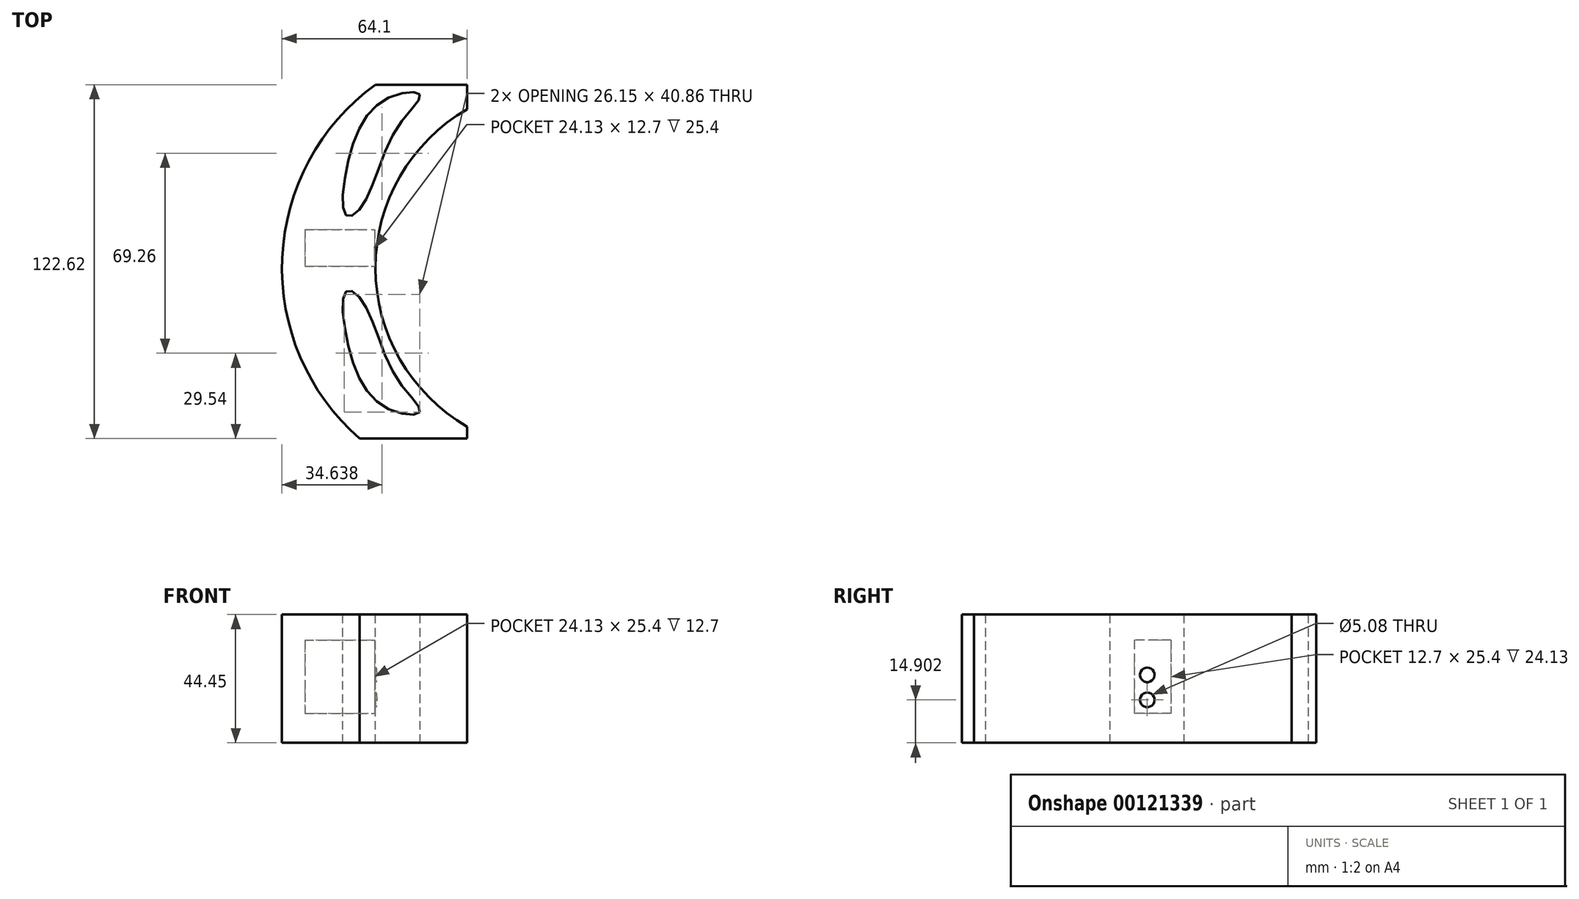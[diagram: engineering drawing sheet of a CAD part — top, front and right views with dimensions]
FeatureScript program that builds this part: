
annotation { "Feature Type Name" : "Feature", "Feature Type Description" : "" }
export const myFeature = defineFeature(function(context is Context, id is Id, definition is map)
    precondition{}
    {
        {
            var Q0;
            Q0=qCreatedBy(makeId("Top.planeOp"),FACE);
            var sketch = newSketch(context, id + "F0", { "sketchPlane" : qUnion([Q0])});
            skLineSegment(sketch, "E0.bottom", {"start": v(-63.24, 58.45) * mm, "end": v(63.76, 58.45) * mm});
            skLineSegment(sketch, "E0.top", {"start": v(-63.24, -68.55) * mm, "end": v(63.76, -68.55) * mm});
            skLineSegment(sketch, "E0.left", {"start": v(-63.24, 58.45) * mm, "end": v(-63.24, -68.55) * mm});
            skLineSegment(sketch, "E0.right", {"start": v(63.76, 58.45) * mm, "end": v(63.76, -68.55) * mm});
            skSolve(sketch);
        }
        {
            var Q0;
            Q0 = qSketchRegion(id + "F0", true);
            extrude(context, id + "F1", {"entities" : qUnion([Q0]), "depth" : 44.45 * mm});
        }
        {
            var Q0;
            Q0=makeQuery(id+"F1.opExtrude","CAP_FACE",FACE,{"disambiguationData":[OSD([sQuery(id+"F0.wireOp",EDGE,"E0.bottom"),sQuery(id+"F0.wireOp",EDGE,"E0.top"),sQuery(id+"F0.wireOp",EDGE,"E0.left"),sQuery(id+"F0.wireOp",EDGE,"E0.right")])],"isStart":false});
            var sketch = newSketch(context, id + "F2", { "sketchPlane" : qUnion([Q0])});
            skPoint(sketch, "E1.startSnap0", {"position": v(0.26, 58.45) * mm});
            skLineSegment(sketch, "E2", {"start": v(-63.24, 58.45) * mm, "end": v(-63.24, -68.55) * mm});
            skLineSegment(sketch, "E3", {"start": v(-63.24, -68.55) * mm, "end": v(0.26, -68.55) * mm});
            skArc(sketch, "E4", {"start": v(0.26, 58.45) * mm, "mid": v(-32.09, -5.05) * mm, "end": v(0.26, -68.55) * mm});
            skLineSegment(sketch, "E5", {"start": v(-63.24, 58.45) * mm, "end": v(0.26, 58.45) * mm});
            skSolve(sketch);
        }
        {
            var Q0;
            Q0 = qSketchRegion(id + "F2", true);
            var Q1;
            Q1=makeQuery(id+"F1.opExtrude","CAP_FACE",FACE,{"disambiguationData":[OSD([sQuery(id+"F0.wireOp",EDGE,"E0.bottom"),sQuery(id+"F0.wireOp",EDGE,"E0.top"),sQuery(id+"F0.wireOp",EDGE,"E0.left"),sQuery(id+"F0.wireOp",EDGE,"E0.right")])],"isStart":true});
            extrude(context, id + "F3", {"entities" : qUnion([Q0]), "operationType" : NewBodyOperationType.REMOVE, "endBound" : BoundingType.UP_TO_SURFACE, "oppositeDirection" : true, "endBoundEntityFace" : qUnion([Q1]), "depth" : 25.4 * mm});
        }
        {
            var Q0;
            Q0=makeQuery(id+"F1.opExtrude","CAP_FACE",FACE,{"disambiguationData":[OSD([sQuery(id+"F0.wireOp",EDGE,"E0.bottom"),sQuery(id+"F0.wireOp",EDGE,"E0.top"),sQuery(id+"F0.wireOp",EDGE,"E0.left"),sQuery(id+"F0.wireOp",EDGE,"E0.right")])],"isStart":false});
            var sketch = newSketch(context, id + "F4", { "sketchPlane" : qUnion([Q0])});
            skArc(sketch, "E6", {"start": v(63.76, 58.45) * mm, "mid": v(0.26, -5.05) * mm, "end": v(63.76, -68.55) * mm});
            skLineSegment(sketch, "E7", {"start": v(63.76, -68.55) * mm, "end": v(63.76, 58.45) * mm});
            skSolve(sketch);
        }
        {
            var Q0;
            Q0 = qSketchRegion(id + "F4", true);
            var Q1;
            Q1=makeQuery(id+"F1.opExtrude","CAP_FACE",FACE,{"disambiguationData":[OSD([sQuery(id+"F0.wireOp",EDGE,"E0.bottom"),sQuery(id+"F0.wireOp",EDGE,"E0.top"),sQuery(id+"F0.wireOp",EDGE,"E0.left"),sQuery(id+"F0.wireOp",EDGE,"E0.right")])],"isStart":true});
            extrude(context, id + "F5", {"entities" : qUnion([Q0]), "operationType" : NewBodyOperationType.REMOVE, "endBound" : BoundingType.UP_TO_SURFACE, "oppositeDirection" : true, "endBoundEntityFace" : qUnion([Q1]), "depth" : 25.4 * mm});
        }
        {
            var Q0;
            Q0=makeQuery(id+"F1.opExtrude","CAP_FACE",FACE,{"disambiguationData":[OSD([sQuery(id+"F0.wireOp",EDGE,"E0.bottom"),sQuery(id+"F0.wireOp",EDGE,"E0.top"),sQuery(id+"F0.wireOp",EDGE,"E0.left"),sQuery(id+"F0.wireOp",EDGE,"E0.right")])],"isStart":false});
            var sketch = newSketch(context, id + "F6", { "sketchPlane" : qUnion([Q0])});
            skLineSegment(sketch, "E8.bottom", {"start": v(45.03, -99.41) * mm, "end": v(83.6, -99.41) * mm});
            skLineSegment(sketch, "E8.top", {"start": v(45.03, 124.65) * mm, "end": v(83.6, 124.65) * mm});
            skLineSegment(sketch, "E8.left", {"start": v(45.03, -99.41) * mm, "end": v(45.03, 124.65) * mm});
            skLineSegment(sketch, "E8.right", {"start": v(83.6, -99.41) * mm, "end": v(83.6, 124.65) * mm});
            skSolve(sketch);
        }
        {
            var Q0;
            {var subQ1=sQuery(id+"F6.wireOp",EDGE,"E8.bottom");Q0=makeQuery(id+"F6.imprint","IMPRINT",FACE,{"disambiguationData":[TD([[makeQuery(id+"F6.imprint","IMPRINT",EDGE,{"derivedFrom":subQ1}),1.0]])]});}
            extrude(context, id + "F7", {"entities" : qUnion([Q0]), "operationType" : NewBodyOperationType.REMOVE, "oppositeDirection" : true, "depth" : 46.07 * mm});
        }
        {
            var Q0;
            Q0=makeQuery(id+"F1.opExtrude","CAP_FACE",FACE,{"disambiguationData":[OSD([sQuery(id+"F0.wireOp",EDGE,"E0.bottom"),sQuery(id+"F0.wireOp",EDGE,"E0.top"),sQuery(id+"F0.wireOp",EDGE,"E0.left"),sQuery(id+"F0.wireOp",EDGE,"E0.right")])],"isStart":false});
            var sketch = newSketch(context, id + "F8", { "sketchPlane" : qUnion([Q0])});
            skLineSegment(sketch, "E9.bottom", {"start": v(32.01, -68.55) * mm, "end": v(64.03, -68.55) * mm});
            skLineSegment(sketch, "E9.top", {"start": v(32.01, -59.64) * mm, "end": v(64.03, -59.64) * mm});
            skLineSegment(sketch, "E9.left", {"start": v(32.01, -68.55) * mm, "end": v(32.01, -59.64) * mm});
            skLineSegment(sketch, "E9.right", {"start": v(64.03, -68.55) * mm, "end": v(64.03, -59.64) * mm});
            skSolve(sketch);
        }
        {
            var Q0;
            Q0 = qSketchRegion(id + "F8", true);
            var Q1;
            Q1=makeQuery(id+"F1.opExtrude","CAP_FACE",FACE,{"disambiguationData":[OSD([sQuery(id+"F0.wireOp",EDGE,"E0.bottom"),sQuery(id+"F0.wireOp",EDGE,"E0.top"),sQuery(id+"F0.wireOp",EDGE,"E0.left"),sQuery(id+"F0.wireOp",EDGE,"E0.right")])],"isStart":true});
            extrude(context, id + "F9", {"entities" : qUnion([Q0]), "operationType" : NewBodyOperationType.REMOVE, "endBound" : BoundingType.UP_TO_SURFACE, "oppositeDirection" : true, "endBoundEntityFace" : qUnion([Q1]), "depth" : 25.4 * mm});
        }
        {
            var Q0;
            Q0=makeQuery(id+"F1.opExtrude","CAP_FACE",FACE,{"disambiguationData":[OSD([sQuery(id+"F0.wireOp",EDGE,"E0.bottom"),sQuery(id+"F0.wireOp",EDGE,"E0.top"),sQuery(id+"F0.wireOp",EDGE,"E0.left"),sQuery(id+"F0.wireOp",EDGE,"E0.right")])],"isStart":false});
            var sketch = newSketch(context, id + "F10", { "sketchPlane" : qUnion([Q0])});
            skLineSegment(sketch, "E10.bottom", {"start": v(32.01, 58.45) * mm, "end": v(63.76, 58.45) * mm});
            skLineSegment(sketch, "E10.top", {"start": v(32.01, 38.53) * mm, "end": v(63.76, 38.53) * mm});
            skLineSegment(sketch, "E10.left", {"start": v(32.01, 58.45) * mm, "end": v(32.01, 38.53) * mm});
            skLineSegment(sketch, "E10.right", {"start": v(63.76, 58.45) * mm, "end": v(63.76, 38.53) * mm});
            skSolve(sketch);
        }
        {
            var Q0;
            Q0 = qSketchRegion(id + "F10", true);
            var Q1;
            Q1=makeQuery(id+"F1.opExtrude","CAP_FACE",FACE,{"disambiguationData":[OSD([sQuery(id+"F0.wireOp",EDGE,"E0.bottom"),sQuery(id+"F0.wireOp",EDGE,"E0.top"),sQuery(id+"F0.wireOp",EDGE,"E0.left"),sQuery(id+"F0.wireOp",EDGE,"E0.right")])],"isStart":true});
            extrude(context, id + "F11", {"entities" : qUnion([Q0]), "operationType" : NewBodyOperationType.REMOVE, "endBound" : BoundingType.UP_TO_SURFACE, "oppositeDirection" : true, "endBoundEntityFace" : qUnion([Q1]), "depth" : 25.4 * mm});
        }
        {
            var Q0;
            Q0=qCreatedBy(makeId("Right.planeOp"),FACE);
            var sketch = newSketch(context, id + "F12", { "sketchPlane" : qUnion([Q0])});
            skLineSegment(sketch, "E11.bottom", {"start": v(8.2, 35.56) * mm, "end": v(-4.5, 35.56) * mm});
            skLineSegment(sketch, "E11.top", {"start": v(8.2, 10.16) * mm, "end": v(-4.5, 10.16) * mm});
            skLineSegment(sketch, "E11.left", {"start": v(8.2, 35.56) * mm, "end": v(8.2, 10.16) * mm});
            skLineSegment(sketch, "E11.right", {"start": v(-4.5, 35.56) * mm, "end": v(-4.5, 10.16) * mm});
            skSolve(sketch);
        }
        {
            var Q0;
            Q0 = qSketchRegion(id + "F12", true);
            var Q1;
            Q1=makeQuery(id+"F3.boolean.opBoolean","COPY",FACE,{"derivedFrom":makeQuery(id+"F3.opExtrude","SWEPT_FACE",FACE,{"disambiguationData":[OSD([sQuery(id+"F2.wireOp",EDGE,"E1")])]})});
            extrude(context, id + "F13", {"entities" : qUnion([Q0]), "operationType" : NewBodyOperationType.REMOVE, "oppositeDirection" : true, "endBoundEntityFace" : qUnion([Q1]), "depth" : 24.13 * mm});
        }
        {
            var Q0;
            Q0=makeQuery(id+"F13.boolean.opBoolean","COPY",FACE,{"derivedFrom":makeQuery(id+"F13.opExtrude","CAP_FACE",FACE,{"disambiguationData":[OSD([sQuery(id+"F12.wireOp",EDGE,"E11.bottom"),sQuery(id+"F12.wireOp",EDGE,"E11.top"),sQuery(id+"F12.wireOp",EDGE,"E11.left"),sQuery(id+"F12.wireOp",EDGE,"E11.right")])],"isStart":true})});
            var sketch = newSketch(context, id + "F14", { "sketchPlane" : qUnion([Q0])});
            skCircle(sketch, "E12", {"center": v(0, 14.9) * mm, "radius": 2.54 * mm});
            skCircle(sketch, "E13", {"center": v(0, 23.56) * mm, "radius": 2.53 * mm});
            skSolve(sketch);
        }
        {
            var Q0;
            Q0 = qSketchRegion(id + "F14", true);
            extrude(context, id + "F15", {"entities" : qUnion([Q0]), "operationType" : NewBodyOperationType.REMOVE, "oppositeDirection" : true, "depth" : 25.4 * mm});
        }
        {
            var Q0;
            Q0=makeQuery(id+"F1.opExtrude","CAP_FACE",FACE,{"disambiguationData":[OSD([sQuery(id+"F0.wireOp",EDGE,"E0.bottom"),sQuery(id+"F0.wireOp",EDGE,"E0.top"),sQuery(id+"F0.wireOp",EDGE,"E0.left"),sQuery(id+"F0.wireOp",EDGE,"E0.right")])],"isStart":true});
            var sketch = newSketch(context, id + "F16", { "sketchPlane" : qUnion([Q0])});
            skFitSpline(sketch, "E14", {"points": [v(15.62, -55.06) * mm, v(3.77, -53.45) * mm, v(-8.86, -33.07) * mm, v(-9.85, -13.16) * mm, v(-4.4, -16.29) * mm, v(7.7, -43.33) * mm, v(15.62, -55.06) * mm]});
            skFitSpline(sketch, "E15.MirrorC", {"points": [v(15.62, 55.06) * mm, v(3.77, 53.45) * mm, v(-8.86, 33.07) * mm, v(-9.85, 13.16) * mm, v(-4.4, 16.29) * mm, v(7.7, 43.33) * mm, v(15.62, 55.06) * mm]});
            skSolve(sketch);
        }
        {
            var Q0;
            Q0 = qSketchRegion(id + "F16", true);
            extrude(context, id + "F17", {"entities" : qUnion([Q0]), "operationType" : NewBodyOperationType.REMOVE, "endBound" : BoundingType.UP_TO_NEXT, "oppositeDirection" : true, "depth" : 25.4 * mm});
        }
        {
            var Q0;
            Q0=makeQuery(id+"F1.opExtrude","CAP_FACE",FACE,{"disambiguationData":[OSD([sQuery(id+"F0.wireOp",EDGE,"E0.bottom"),sQuery(id+"F0.wireOp",EDGE,"E0.top"),sQuery(id+"F0.wireOp",EDGE,"E0.left"),sQuery(id+"F0.wireOp",EDGE,"E0.right")])],"isStart":false});
            var sketch = newSketch(context, id + "F18", { "sketchPlane" : qUnion([Q0])});
            skLineSegment(sketch, "E16.bottom", {"start": v(32.01, -68.55) * mm, "end": v(-12.9, -68.55) * mm});
            skLineSegment(sketch, "E16.top", {"start": v(32.01, -64.17) * mm, "end": v(-12.9, -64.17) * mm});
            skLineSegment(sketch, "E16.left", {"start": v(32.01, -68.55) * mm, "end": v(32.01, -64.17) * mm});
            skLineSegment(sketch, "E16.right", {"start": v(-12.9, -68.55) * mm, "end": v(-12.9, -64.17) * mm});
            skSolve(sketch);
        }
        {
            var Q0;
            Q0 = qSketchRegion(id + "F18", true);
            var Q1;
            Q1=makeQuery(id+"F1.opExtrude","CAP_FACE",FACE,{"disambiguationData":[OSD([sQuery(id+"F0.wireOp",EDGE,"E0.bottom"),sQuery(id+"F0.wireOp",EDGE,"E0.top"),sQuery(id+"F0.wireOp",EDGE,"E0.left"),sQuery(id+"F0.wireOp",EDGE,"E0.right")])],"isStart":true});
            extrude(context, id + "F19", {"entities" : qUnion([Q0]), "operationType" : NewBodyOperationType.REMOVE, "endBound" : BoundingType.UP_TO_SURFACE, "oppositeDirection" : true, "endBoundEntityFace" : qUnion([Q1]), "depth" : 25.4 * mm});
        }
        {
            var Q0;
            Q0 = qSketchRegion(id + "F2", true);
            extrude(context, id + "F20", {"entities" : qUnion([Q0]), "operationType" : NewBodyOperationType.REMOVE, "oppositeDirection" : true, "depth" : 25 * mm});
        }
    });
